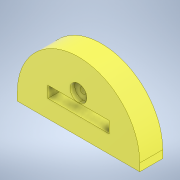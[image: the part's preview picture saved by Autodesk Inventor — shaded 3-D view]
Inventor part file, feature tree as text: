
AUTODESK INVENTOR PART (.ipt)
format: ipt  version: 2021.1 (Build 251245000, 245)  size: 165,376 bytes
history: native  units: in
note: dims shown in document units (in); Inventor stores cm internally (conversion verified against a paired STEP export)
features: sketch x3, extrude x3, hole x1
ambient origin geometry x8: Origin, YZ Plane, XZ Plane, XY Plane, X Axis, Y Axis, Z Axis, Center Point
bodies: Solid1 (feature_tree)
feature tree (7):
  sketch  "Sketch2"  dims[d2=2.5in d3=0.375in]
  extrude  "Extrusion1"  Depth=0.375in
  extrude  "Extrusion2"  Depth=1.0in
  hole  "Hole2"  [1 undecoded]
  extrude  "Extrusion3"  Depth=0.25in TaperAngle=0.0deg
  sketch  "Sketch5"  dims[d4=0.375in d5=1.0in]
  sketch  "Sketch6"  dims[d6=0.325in d7=0.375in d8=0.25in d9=0.0in d10=0.5in d11=0.0in d20=0.201in d21=0.75in d22=0.55in d23=0.15in d24=0.5635in d25=1.0in d26=0.0in d27=0.25in d28=0.0in]
note: 1 required parameter value undecoded (feature->parameter linkage not recoverable at this tier; creation-order binding heuristic only, values carry confidence <= 0.55)
